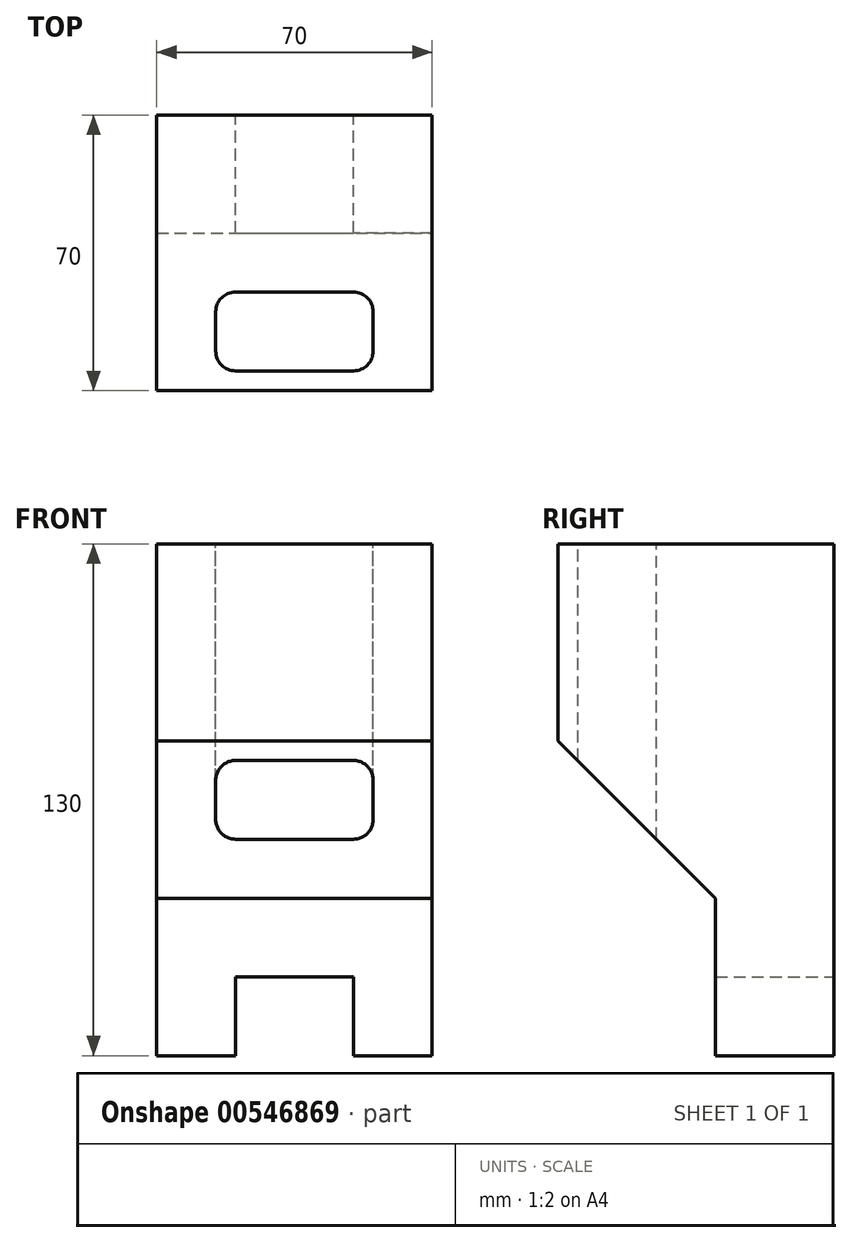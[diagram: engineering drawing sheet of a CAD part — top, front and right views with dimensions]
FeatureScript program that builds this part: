
annotation { "Feature Type Name" : "Feature", "Feature Type Description" : "" }
export const myFeature = defineFeature(function(context is Context, id is Id, definition is map)
    precondition{}
    {
        {
            var Q0;
            Q0=qCreatedBy(makeId("Front.planeOp"),FACE);
            var sketch = newSketch(context, id + "F0", { "sketchPlane" : qUnion([Q0])});
            skLineSegment(sketch, "E0.bottom", {"start": v(35, 65) * mm, "end": v(-35, 65) * mm});
            skLineSegment(sketch, "E0.top", {"start": v(35, -65) * mm, "end": v(15, -65) * mm});
            skLineSegment(sketch, "E0.left", {"start": v(35, 65) * mm, "end": v(35, -65) * mm});
            skLineSegment(sketch, "E0.right", {"start": v(-35, 65) * mm, "end": v(-35, -65) * mm});
            skPoint(sketch, "E0.middle", {"position": v(0, 0) * mm});
            skLineSegment(sketch, "E1", {"start": v(-35, -65) * mm, "end": v(-35, -45) * mm});
            skLineSegment(sketch, "E2", {"start": v(35, -65) * mm, "end": v(35, -45) * mm});
            skLineSegment(sketch, "E3", {"start": v(-35, -65) * mm, "end": v(-15, -65) * mm});
            skLineSegment(sketch, "E4", {"start": v(-15, -65) * mm, "end": v(-15, -45) * mm});
            skLineSegment(sketch, "E5", {"start": v(15, -65) * mm, "end": v(15, -45) * mm});
            skLineSegment(sketch, "E6", {"start": v(-15, -45) * mm, "end": v(15, -45) * mm});
            skLineSegment(sketch, "E7.trimOffspring", {"start": v(-15, -65) * mm, "end": v(-35, -65) * mm});
            skSolve(sketch);
        }
        {
            var Q0;
            Q0 = qSketchRegion(id + "F0", true);
            extrude(context, id + "F1", {"entities" : qUnion([Q0]), "depth" : 30 * mm, "offsetDistance" : 25 * mm});
        }
        {
            var Q0;
            Q0=makeQuery(id+"F1.opExtrude","CAP_FACE",FACE,{"disambiguationData":[OSD([sQuery(id+"F0.wireOp",EDGE,"E0.bottom"),sQuery(id+"F0.wireOp",EDGE,"E0.left"),sQuery(id+"F0.wireOp",EDGE,"E0.right"),sQuery(id+"F0.wireOp",EDGE,"E1"),sQuery(id+"F0.wireOp",EDGE,"E2"),sQuery(id+"F0.wireOp",EDGE,"E0.top"),sQuery(id+"F0.wireOp",EDGE,"E4"),sQuery(id+"F0.wireOp",EDGE,"E5"),sQuery(id+"F0.wireOp",EDGE,"E6"),sQuery(id+"F0.wireOp",EDGE,"E7.trimOffspring")])],"isStart":false});
            var sketch = newSketch(context, id + "F2", { "sketchPlane" : qUnion([Q0])});
            skLineSegment(sketch, "E8", {"start": v(-35, 65) * mm, "end": v(-35, 15) * mm});
            skLineSegment(sketch, "E9", {"start": v(-35, 15) * mm, "end": v(35, 15) * mm});
            skLineSegment(sketch, "E10", {"start": v(35, 15) * mm, "end": v(35, 65) * mm});
            skLineSegment(sketch, "E11", {"start": v(-35, 65) * mm, "end": v(35, 65) * mm});
            skLineSegment(sketch, "E12", {"start": v(-35, 15) * mm, "end": v(-35, 30) * mm});
            skLineSegment(sketch, "E13", {"start": v(-35, 65) * mm, "end": v(-35, 50) * mm});
            skLineSegment(sketch, "E14", {"start": v(-35, 65) * mm, "end": v(-20, 65) * mm});
            skLineSegment(sketch, "E15", {"start": v(35, 65) * mm, "end": v(20, 65) * mm});
            skLineSegment(sketch, "E16", {"start": v(35, 15) * mm, "end": v(20, 15) * mm});
            skLineSegment(sketch, "E17", {"start": v(-35, 15) * mm, "end": v(-20, 15) * mm});
            skLineSegment(sketch, "E18", {"start": v(35, 65) * mm, "end": v(35, 50) * mm});
            skLineSegment(sketch, "E19", {"start": v(35, 15) * mm, "end": v(35, 30) * mm});
            skSolve(sketch);
        }
        {
            var Q0;
            Q0=makeQuery(id+"F2.imprint","IMPRINT",FACE,{"disambiguationData":[TD([[makeQuery(id+"F2.imprint","IMPRINT",EDGE,{"derivedFrom":sQuery(id+"F2.wireOp",EDGE,"E8")}),1.0]])]});
            extrude(context, id + "F3", {"entities" : qUnion([Q0]), "operationType" : NewBodyOperationType.ADD, "depth" : 40 * mm, "offsetDistance" : 25 * mm});
        }
        {
            var Q0;
            Q0=makeQuery(id+"F3.boolean.opBoolean","MERGE",FACE,{"derivedFrom":[makeQuery(id+"F1.opExtrude","SWEPT_FACE",FACE,{"disambiguationData":[OSD([sQuery(id+"F0.wireOp",EDGE,"E0.left"),sQuery(id+"F0.wireOp",EDGE,"E2")])]}),makeQuery(id+"F3.opExtrude","SWEPT_FACE",FACE,{"disambiguationData":[OSD([sQuery(id+"F2.wireOp",EDGE,"E10")])]})]});
            var sketch = newSketch(context, id + "F4", { "sketchPlane" : qUnion([Q0])});
            skLineSegment(sketch, "E20", {"start": v(-30, -65) * mm, "end": v(-30, -25) * mm});
            skLineSegment(sketch, "E21", {"start": v(-30, -25) * mm, "end": v(-70, 15) * mm});
            skSolve(sketch);
        }
        {
            var Q0;
            {var subQ0=sQuery(id+"F4.wireOp",EDGE,"E21");Q0=makeQuery(id+"F4.imprint","IMPRINT",FACE,{"disambiguationData":[TD([[makeQuery(id+"F4.imprint","IMPRINT",EDGE,{"derivedFrom":subQ0}),-1.0]])]});}
            extrude(context, id + "F5", {"entities" : qUnion([Q0]), "operationType" : NewBodyOperationType.ADD, "oppositeDirection" : true, "depth" : 70 * mm, "offsetDistance" : 25 * mm});
        }
        {
            var Q0;
            Q0=makeQuery(id+"F3.boolean.opBoolean","MERGE",FACE,{"derivedFrom":[makeQuery(id+"F1.opExtrude","SWEPT_FACE",FACE,{"disambiguationData":[OSD([sQuery(id+"F0.wireOp",EDGE,"E0.bottom")])]}),makeQuery(id+"F3.opExtrude","SWEPT_FACE",FACE,{"disambiguationData":[OSD([sQuery(id+"F2.wireOp",EDGE,"E11"),sQuery(id+"F2.wireOp",EDGE,"E14"),sQuery(id+"F2.wireOp",EDGE,"E15")])]})]});
            var sketch = newSketch(context, id + "F6", { "sketchPlane" : qUnion([Q0])});
            skLineSegment(sketch, "E22", {"start": v(-35, 0) * mm, "end": v(-35, -40) * mm});
            skLineSegment(sketch, "E23", {"start": v(35, 0) * mm, "end": v(35, -40) * mm});
            skLineSegment(sketch, "E24", {"start": v(-35, -40) * mm, "end": v(-35, -45) * mm});
            skLineSegment(sketch, "E25", {"start": v(35, -40) * mm, "end": v(35, -45) * mm});
            skLineSegment(sketch, "E26", {"start": v(-35, -70) * mm, "end": v(-35, -65) * mm});
            skLineSegment(sketch, "E27", {"start": v(35, -70) * mm, "end": v(35, -65) * mm});
            skLineSegment(sketch, "E28", {"start": v(-35, -70) * mm, "end": v(-20, -70) * mm});
            skLineSegment(sketch, "E29", {"start": v(35, -70) * mm, "end": v(20, -70) * mm});
            skLineSegment(sketch, "E30", {"start": v(-15, -45) * mm, "end": v(15, -45) * mm});
            skLineSegment(sketch, "E31", {"start": v(-15, -65) * mm, "end": v(15, -65) * mm});
            skLineSegment(sketch, "E32", {"start": v(-35, -40) * mm, "end": v(35, -40) * mm});
            skLineSegment(sketch, "E33", {"start": v(-20, -60) * mm, "end": v(-20, -50) * mm});
            skLineSegment(sketch, "E34", {"start": v(20, -60) * mm, "end": v(20, -50) * mm});
            skPoint(sketch, "E35.endSnap0", {"position": v(0, -65) * mm});
            skPoint(sketch, "E35.end.orphan", {"position": v(0, -55) * mm});
            skPoint(sketch, "E35.start.orphan", {"position": v(0, -45) * mm});
            skPoint(sketch, "E36.newPointA", {"position": v(20, -45) * mm});
            skPoint(sketch, "E36.newPointB", {"position": v(20, -40) * mm});
            skArc(sketch, "E36.filletArc", {"start": v(20, -50) * mm, "mid": v(18.54, -46.46) * mm, "end": v(15, -45) * mm});
            skPoint(sketch, "E37.newPointA", {"position": v(20, -65) * mm});
            skArc(sketch, "E37.filletArc", {"start": v(15, -65) * mm, "mid": v(18.54, -63.54) * mm, "end": v(20, -60) * mm});
            skPoint(sketch, "E38.newPointA", {"position": v(-20, -65) * mm});
            skArc(sketch, "E38.filletArc", {"start": v(-20, -60) * mm, "mid": v(-18.54, -63.54) * mm, "end": v(-15, -65) * mm});
            skPoint(sketch, "E39.newPointA", {"position": v(-20, -45) * mm});
            skPoint(sketch, "E39.newPointB", {"position": v(-20, -40) * mm});
            skArc(sketch, "E39.filletArc", {"start": v(-15, -45) * mm, "mid": v(-18.54, -46.46) * mm, "end": v(-20, -50) * mm});
            skSolve(sketch);
        }
        {
            var Q0;
            Q0 = qSketchRegion(id + "F6", true);
            extrude(context, id + "F7", {"entities" : qUnion([Q0]), "operationType" : NewBodyOperationType.REMOVE, "endBound" : BoundingType.THROUGH_ALL, "oppositeDirection" : true, "depth" : 25 * mm, "offsetDistance" : 25 * mm});
        }
    });
